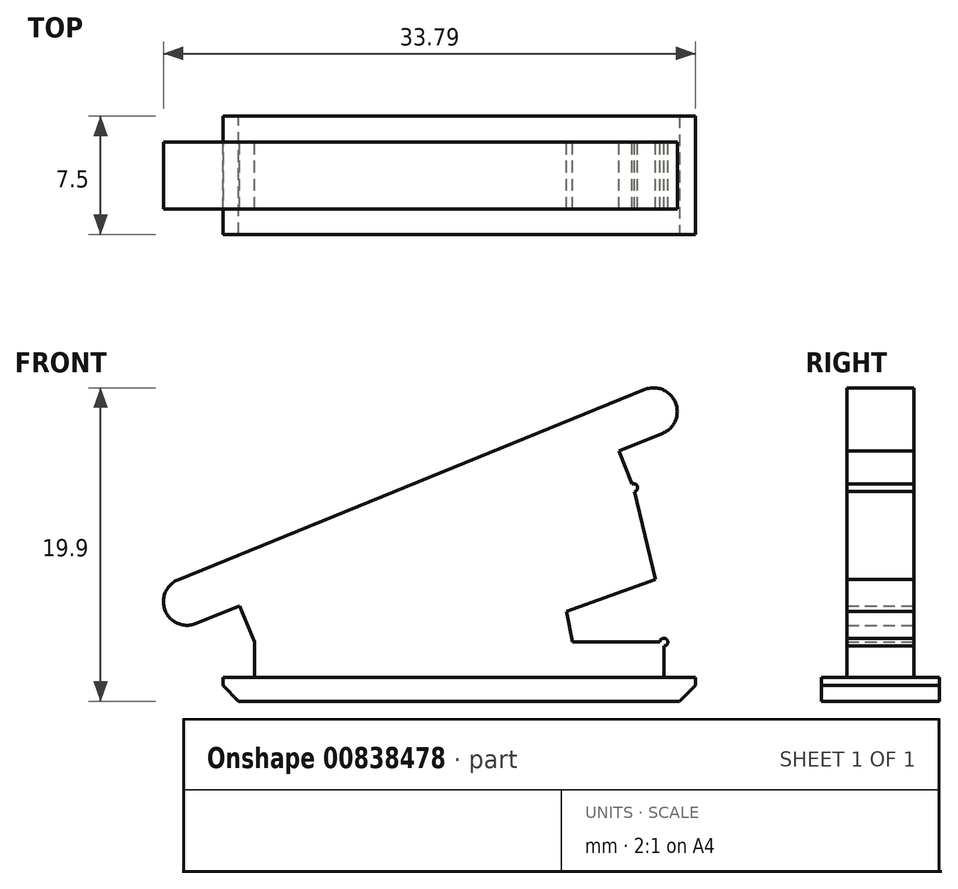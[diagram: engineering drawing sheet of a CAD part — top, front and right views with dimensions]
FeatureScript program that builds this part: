
annotation { "Feature Type Name" : "Feature", "Feature Type Description" : "" }
export const myFeature = defineFeature(function(context is Context, id is Id, definition is map)
    precondition{}
    {
        {
            var Q0;
            Q0=qCreatedBy(makeId("Front.planeOp"),FACE);
            var sketch = newSketch(context, id + "F0", { "sketchPlane" : qUnion([Q0])});
            skLineSegment(sketch, "E0", {"start": v(-15.21, 0) * mm, "end": v(14.79, 0) * mm});
            skLineSegment(sketch, "E1", {"start": v(14.79, 0) * mm, "end": v(14.79, 1.5) * mm});
            skLineSegment(sketch, "E2", {"start": v(14.79, 1.5) * mm, "end": v(12.79, 1.5) * mm});
            skLineSegment(sketch, "E3", {"start": v(12.79, 1.5) * mm, "end": v(12.79, 3.75) * mm});
            skLineSegment(sketch, "E4", {"start": v(-13.21, 3.75) * mm, "end": v(-13.21, 1.5) * mm});
            skLineSegment(sketch, "E5", {"start": v(-13.21, 1.5) * mm, "end": v(-15.21, 1.5) * mm});
            skLineSegment(sketch, "E6", {"start": v(-15.21, 1.5) * mm, "end": v(-15.21, 0) * mm});
            skLineSegment(sketch, "E7", {"start": v(-13.21, 1.5) * mm, "end": v(12.79, 1.5) * mm});
            skLineSegment(sketch, "E8", {"start": v(-13.21, 3.75) * mm, "end": v(-14.16, 6.07) * mm});
            skLineSegment(sketch, "E9", {"start": v(9.92, 15.88) * mm, "end": v(10.86, 13.56) * mm});
            skLineSegment(sketch, "E10", {"start": v(9.92, 15.88) * mm, "end": v(12.7, 17.01) * mm});
            skLineSegment(sketch, "E11", {"start": v(13.52, 18.97) * mm, "end": v(13.52, 18.97) * mm});
            skLineSegment(sketch, "E12", {"start": v(11.57, 19.79) * mm, "end": v(-18.07, 7.71) * mm});
            skLineSegment(sketch, "E13", {"start": v(-18.9, 5.76) * mm, "end": v(-18.9, 5.76) * mm});
            skLineSegment(sketch, "E14", {"start": v(-16.94, 4.93) * mm, "end": v(-14.16, 6.07) * mm});
            skPoint(sketch, "E15.visualSharp", {"position": v(-19.46, 7.14) * mm});
            skArc(sketch, "E15.filletArc", {"start": v(-18.07, 7.71) * mm, "mid": v(-18.88, 6.9) * mm, "end": v(-18.9, 5.76) * mm});
            skPoint(sketch, "E16.visualSharp", {"position": v(-18.32, 4.37) * mm});
            skArc(sketch, "E16.filletArc", {"start": v(-18.9, 5.76) * mm, "mid": v(-18.08, 4.94) * mm, "end": v(-16.94, 4.93) * mm});
            skPoint(sketch, "E17.visualSharp", {"position": v(12.95, 20.36) * mm});
            skArc(sketch, "E17.filletArc", {"start": v(13.52, 18.97) * mm, "mid": v(12.71, 19.78) * mm, "end": v(11.57, 19.79) * mm});
            skPoint(sketch, "E18.visualSharp", {"position": v(14.09, 17.58) * mm});
            skArc(sketch, "E18.filletArc", {"start": v(12.7, 17.01) * mm, "mid": v(13.51, 17.82) * mm, "end": v(13.52, 18.97) * mm});
            skLineSegment(sketch, "E19", {"start": v(6.6, 5.71) * mm, "end": v(6.98, 3.75) * mm});
            skPoint(sketch, "E20.visualSharp", {"position": v(12.25, 7.73) * mm});
            skCircle(sketch, "E21", {"center": v(10.86, 13.56) * mm, "radius": 0.25 * mm});
            skLineSegment(sketch, "E22", {"start": v(6.98, 3.75) * mm, "end": v(12.79, 3.75) * mm});
            skCircle(sketch, "E23", {"center": v(12.79, 3.75) * mm, "radius": 0.25 * mm});
            skLineSegment(sketch, "E24", {"start": v(6.6, 5.71) * mm, "end": v(12.25, 7.73) * mm});
            skLineSegment(sketch, "E25", {"start": v(10.86, 13.56) * mm, "end": v(12.25, 7.73) * mm});
            skSolve(sketch);
        }
        {
            var Q0;
            Q0=makeQuery(id+"F0.imprint","IMPRINT",FACE,{"disambiguationData":[TD([[makeQuery(id+"F0.imprint","IMPRINT",EDGE,{"derivedFrom":sQuery(id+"F0.wireOp",EDGE,"E0")}),1.0]])]});
            extrude(context, id + "F1", {"entities" : qUnion([Q0]), "endBound" : BoundingType.SYMMETRIC, "depth" : 7.5 * mm, "offsetDistance" : 25 * mm});
        }
        {
            var Q0;
            Q0=makeQuery(id+"F0.imprint","IMPRINT",FACE,{"disambiguationData":[TD([[makeQuery(id+"F0.imprint","IMPRINT",EDGE,{"derivedFrom":sQuery(id+"F0.wireOp",EDGE,"E4")}),1.0]])]});
            var Q1;
            {var subQ0=sQuery(id+"F0.wireOp",EDGE,"FaXY5dtp-onB6-Es56-pUMZ-4QwjA434GMjI");var subQ1=sQuery(id+"F0.wireOp",EDGE,"E9");var subQ2=makeQuery(id+"F0.imprint","INTERSECT",VERTEX,{"derivedFrom":[subQ1,subQ0]});Q1=makeQuery(id+"F0.imprint","IMPRINT",FACE,{"disambiguationData":[TD([[makeQuery(id+"F0.imprint","IMPRINT",EDGE,{"disambiguationData":[TD([[subQ2,1.0]])],"derivedFrom":subQ1}),-1.0]])]});}
            var Q2;
            {var subQ0=sQuery(id+"F0.wireOp",EDGE,"FaXY5dtp-onB6-Es56-pUMZ-4QwjA434GMjI");var subQ1=sQuery(id+"F0.wireOp",EDGE,"E9");var subQ2=makeQuery(id+"F0.imprint","INTERSECT",VERTEX,{"derivedFrom":[subQ1,subQ0]});Q2=makeQuery(id+"F0.imprint","IMPRINT",FACE,{"disambiguationData":[TD([[makeQuery(id+"F0.imprint","IMPRINT",EDGE,{"disambiguationData":[TD([[subQ2,1.0]])],"derivedFrom":subQ1}),1.0]])]});}
            var Q3;
            {var subQ0=sQuery(id+"F0.wireOp",EDGE,"E22");var subQ1=sQuery(id+"F0.wireOp",EDGE,"E3");var subQ2=makeQuery(id+"F0.imprint","INTERSECT",VERTEX,{"derivedFrom":[subQ1,subQ0]});Q3=makeQuery(id+"F0.imprint","IMPRINT",FACE,{"disambiguationData":[TD([[makeQuery(id+"F0.imprint","IMPRINT",EDGE,{"disambiguationData":[TD([[subQ2,1.0]])],"derivedFrom":subQ1}),1.0]])]});}
            var Q4;
            {var subQ0=sQuery(id+"F0.wireOp",EDGE,"E22");var subQ1=sQuery(id+"F0.wireOp",EDGE,"E3");var subQ2=makeQuery(id+"F0.imprint","INTERSECT",VERTEX,{"derivedFrom":[subQ1,subQ0]});Q4=makeQuery(id+"F0.imprint","IMPRINT",FACE,{"disambiguationData":[TD([[makeQuery(id+"F0.imprint","IMPRINT",EDGE,{"disambiguationData":[TD([[subQ2,1.0]])],"derivedFrom":subQ1}),-1.0]])]});}
            extrude(context, id + "F2", {"entities" : qUnion([Q0, Q1, Q2, Q3, Q4]), "operationType" : NewBodyOperationType.ADD, "endBound" : BoundingType.SYMMETRIC, "depth" : 4.25 * mm, "offsetDistance" : 25 * mm});
        }
        {
            var Q0;
            Q0=makeQuery(id+"F1.opExtrude","SWEPT_EDGE",EDGE,{"disambiguationData":[OSD([sQuery(id+"F0.wireOp",EDGE,"E0"),sQuery(id+"F0.wireOp",EDGE,"E1")])]});
            var Q1;
            Q1=makeQuery(id+"F1.opExtrude","SWEPT_EDGE",EDGE,{"disambiguationData":[OSD([sQuery(id+"F0.wireOp",EDGE,"E0"),sQuery(id+"F0.wireOp",EDGE,"E6")])]});
            chamfer(context, id + "F3", {"entities" : qUnion([Q0, Q1]), "width" : 1 * mm, "tangentPropagation" : true});
        }
    });
